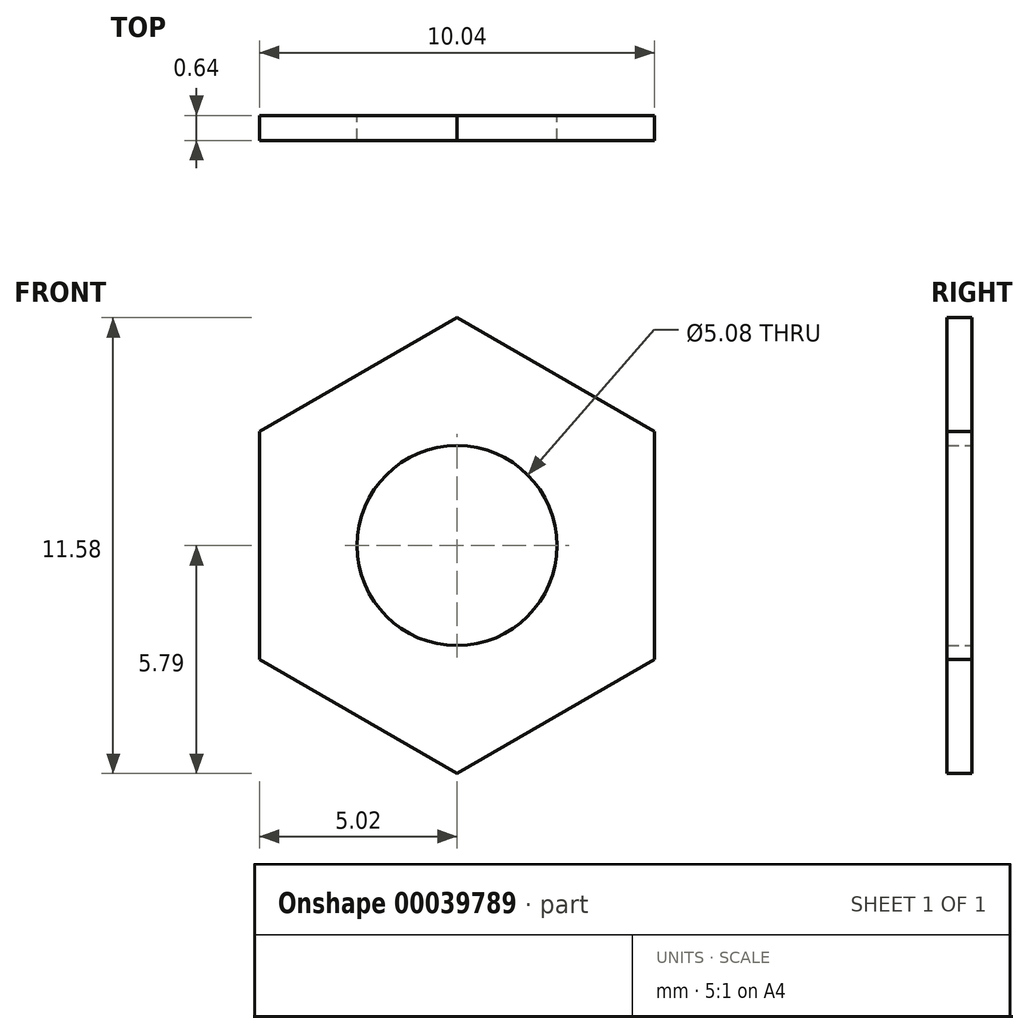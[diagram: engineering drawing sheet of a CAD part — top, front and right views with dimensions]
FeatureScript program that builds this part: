
annotation { "Feature Type Name" : "Feature", "Feature Type Description" : "" }
export const myFeature = defineFeature(function(context is Context, id is Id, definition is map)
    precondition{}
    {
        {
            var Q0;
            Q0=qCreatedBy(makeId("Front.planeOp"),FACE);
            var sketch = newSketch(context, id + "F0", { "sketchPlane" : qUnion([Q0])});
            skLineSegment(sketch, "E0", {"start": v(0, 0) * mm, "end": v(5.02, 0) * mm, "construction": true});
            skCircle(sketch, "E1.cCircle", {"center": v(0, 0) * mm, "radius": 5.02 * mm, "construction": true});
            skLineSegment(sketch, "E1.0", {"start": v(5.02, 2.9) * mm, "end": v(5.02, -2.9) * mm});
            skLineSegment(sketch, "E1.1", {"start": v(5.02, -2.9) * mm, "end": v(0, -5.8) * mm});
            skLineSegment(sketch, "E1.2", {"start": v(0, -5.8) * mm, "end": v(-5.02, -2.9) * mm});
            skLineSegment(sketch, "E1.3", {"start": v(-5.02, -2.9) * mm, "end": v(-5.02, 2.9) * mm});
            skLineSegment(sketch, "E1.4", {"start": v(-5.02, 2.9) * mm, "end": v(0, 5.8) * mm});
            skLineSegment(sketch, "E1.5", {"start": v(0, 5.8) * mm, "end": v(5.02, 2.9) * mm});
            skPoint(sketch, "E1.0.midPoint", {"position": v(5.02, 0) * mm});
            skLineSegment(sketch, "E2", {"start": v(0, 0) * mm, "end": v(2.54, 0) * mm});
            skPoint(sketch, "E3.0.midPoint", {"position": v(2.54, 0) * mm});
            skCircle(sketch, "E4", {"center": v(0, 0) * mm, "radius": 2.54 * mm});
            skSolve(sketch);
        }
        {
            var Q0;
            Q0 = qSketchRegion(id + "F0", true);
            extrude(context, id + "F1", {"entities" : qUnion([Q0]), "depth" : 0.64 * mm});
        }
    });
